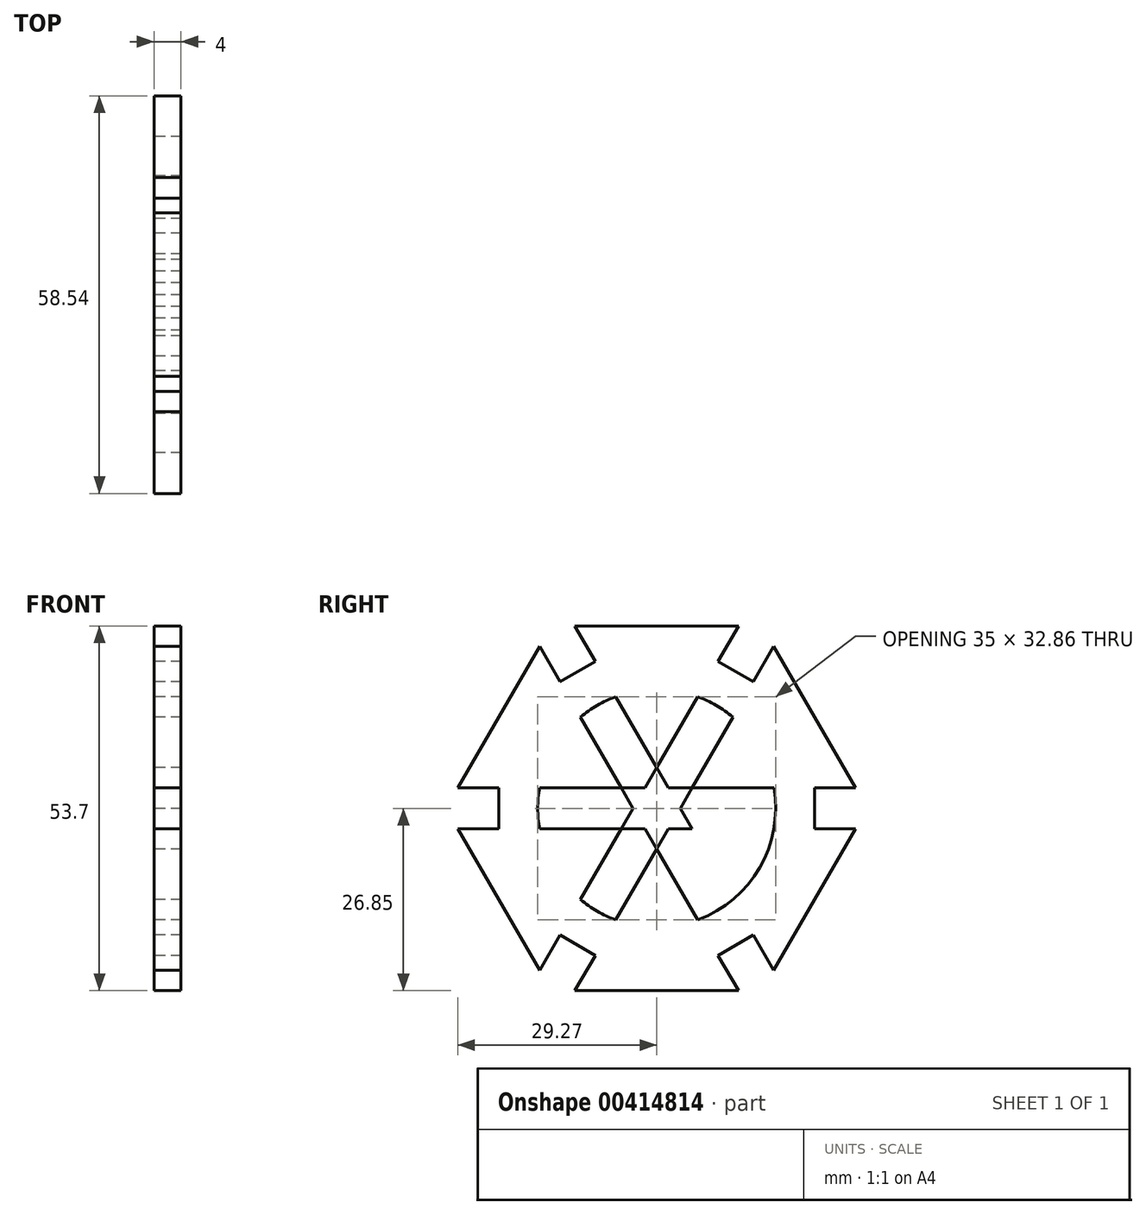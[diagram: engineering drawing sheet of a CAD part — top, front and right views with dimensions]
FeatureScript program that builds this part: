
annotation { "Feature Type Name" : "Feature", "Feature Type Description" : "" }
export const myFeature = defineFeature(function(context is Context, id is Id, definition is map)
    precondition{}
    {
        {
            var Q0;
            Q0=qCreatedBy(makeId("Right.planeOp"),FACE);
            var sketch = newSketch(context, id + "F0", { "sketchPlane" : qUnion([Q0])});
            skCircle(sketch, "E0.cCircle", {"center": v(0, 0) * mm, "radius": 31 * mm, "construction": true});
            skLineSegment(sketch, "E0.0", {"start": v(31, 0) * mm, "end": v(15.5, -26.85) * mm});
            skLineSegment(sketch, "E0.1", {"start": v(15.5, -26.85) * mm, "end": v(-15.5, -26.85) * mm});
            skLineSegment(sketch, "E0.2", {"start": v(-15.5, -26.85) * mm, "end": v(-31, 0) * mm});
            skLineSegment(sketch, "E0.3", {"start": v(-31, 0) * mm, "end": v(-15.5, 26.85) * mm});
            skLineSegment(sketch, "E0.4", {"start": v(-15.5, 26.85) * mm, "end": v(15.5, 26.85) * mm});
            skLineSegment(sketch, "E0.5", {"start": v(15.5, 26.85) * mm, "end": v(31, 0) * mm});
            skLineSegment(sketch, "E1", {"start": v(-31, 0) * mm, "end": v(31, 0) * mm, "construction": true});
            skLineSegment(sketch, "E2", {"start": v(-15.5, 26.85) * mm, "end": v(15.5, -26.85) * mm, "construction": true});
            skLineSegment(sketch, "E3", {"start": v(15.5, 26.85) * mm, "end": v(-15.5, -26.85) * mm, "construction": true});
            skCircle(sketch, "E4.cCircle", {"center": v(0, 0) * mm, "radius": 17.5 * mm});
            skPoint(sketch, "E4.0.midPoint", {"position": v(15.16, 8.75) * mm});
            skLineSegment(sketch, "E5", {"start": v(-11.22, 13.43) * mm, "end": v(6.02, -16.43) * mm});
            skLineSegment(sketch, "E6.MirrorCS", {"start": v(-6.02, 16.43) * mm, "end": v(11.22, -13.43) * mm});
            skLineSegment(sketch, "E7", {"start": v(-17.24, 3) * mm, "end": v(17.24, 3) * mm});
            skLineSegment(sketch, "E8.MirrorCS", {"start": v(-17.24, -3) * mm, "end": v(17.24, -3) * mm});
            skLineSegment(sketch, "E9", {"start": v(-11.22, -13.43) * mm, "end": v(6.02, 16.43) * mm});
            skLineSegment(sketch, "E10.MirrorCS", {"start": v(-6.02, -16.43) * mm, "end": v(11.22, 13.43) * mm});
            skLineSegment(sketch, "E11", {"start": v(-17.23, 23.85) * mm, "end": v(-14.23, 18.65) * mm});
            skLineSegment(sketch, "E12.MirrorCS", {"start": v(-12.04, 26.85) * mm, "end": v(-9.04, 21.65) * mm});
            skLineSegment(sketch, "E13", {"start": v(-14.23, 18.65) * mm, "end": v(-9.04, 21.65) * mm});
            skLineSegment(sketch, "E14.MirrorCS", {"start": v(14.23, 18.65) * mm, "end": v(9.04, 21.65) * mm});
            skLineSegment(sketch, "E15.MirrorCS", {"start": v(17.23, 23.85) * mm, "end": v(14.23, 18.65) * mm});
            skLineSegment(sketch, "E16.MirrorCS", {"start": v(12.04, 26.85) * mm, "end": v(9.04, 21.65) * mm});
            skLineSegment(sketch, "E17.MirrorCS", {"start": v(-12.04, -26.85) * mm, "end": v(-9.04, -21.65) * mm});
            skLineSegment(sketch, "E18.MirrorCS", {"start": v(-14.23, -18.65) * mm, "end": v(-9.04, -21.65) * mm});
            skLineSegment(sketch, "E19.MirrorCS", {"start": v(-17.23, -23.85) * mm, "end": v(-14.23, -18.65) * mm});
            skLineSegment(sketch, "E20.MirrorCS", {"start": v(12.04, -26.85) * mm, "end": v(9.04, -21.65) * mm});
            skLineSegment(sketch, "E21.MirrorCS", {"start": v(14.23, -18.65) * mm, "end": v(9.04, -21.65) * mm});
            skLineSegment(sketch, "E22.MirrorCS", {"start": v(17.23, -23.85) * mm, "end": v(14.23, -18.65) * mm});
            skLineSegment(sketch, "E23", {"start": v(0, 0) * mm, "end": v(-23.25, 13.42) * mm, "construction": true});
            skLineSegment(sketch, "E24.MirrorCS", {"start": v(-29.27, 3) * mm, "end": v(-23.27, 3) * mm});
            skLineSegment(sketch, "E25.MirrorCS", {"start": v(-29.27, -3) * mm, "end": v(-23.27, -3) * mm});
            skLineSegment(sketch, "E26.MirrorCS", {"start": v(-23.27, 3) * mm, "end": v(-23.27, -3) * mm});
            skLineSegment(sketch, "E27.MirrorCS", {"start": v(23.27, 3) * mm, "end": v(23.27, -3) * mm});
            skLineSegment(sketch, "E28.MirrorCS", {"start": v(29.27, -3) * mm, "end": v(23.27, -3) * mm});
            skLineSegment(sketch, "E29.MirrorCS", {"start": v(29.27, 3) * mm, "end": v(23.27, 3) * mm});
            skSolve(sketch);
        }
        {
            var Q0;
            {var subQ4=sQuery(id+"F0.wireOp",EDGE,"E11");Q0=makeQuery(id+"F0.imprint","IMPRINT",FACE,{"disambiguationData":[TD([[makeQuery(id+"F0.imprint","IMPRINT",EDGE,{"derivedFrom":subQ4}),-1.0]])]});}
            var Q1;
            {var subQ1=sQuery(id+"F0.wireOp",EDGE,"E4.cCircle");var subQ5=sQuery(id+"F0.wireOp",EDGE,"E5");var subQ6=makeQuery(id+"F0.imprint","INTERSECT",VERTEX,{"disambiguationData":[OD(0.0)],"derivedFrom":[subQ1,subQ5]});Q1=makeQuery(id+"F0.imprint","IMPRINT",FACE,{"disambiguationData":[TD([[makeQuery(id+"F0.imprint","IMPRINT",EDGE,{"disambiguationData":[TD([[subQ6,1.0]])],"derivedFrom":subQ1}),1.0]])]});}
            var Q2;
            {var subQ5=sQuery(id+"F0.wireOp",EDGE,"E9");var subQ6=sQuery(id+"F0.wireOp",EDGE,"E4.cCircle");var subQ7=makeQuery(id+"F0.imprint","INTERSECT",VERTEX,{"disambiguationData":[OD(1.0)],"derivedFrom":[subQ6,subQ5]});Q2=makeQuery(id+"F0.imprint","IMPRINT",FACE,{"disambiguationData":[TD([[makeQuery(id+"F0.imprint","IMPRINT",EDGE,{"disambiguationData":[TD([[subQ7,1.0]])],"derivedFrom":subQ6}),1.0]])]});}
            var Q3;
            {var subQ5=sQuery(id+"F0.wireOp",EDGE,"E4.cCircle");var subQ7=sQuery(id+"F0.wireOp",EDGE,"E7");var subQ8=makeQuery(id+"F0.imprint","INTERSECT",VERTEX,{"disambiguationData":[OD(1.0)],"derivedFrom":[subQ5,subQ7]});Q3=makeQuery(id+"F0.imprint","IMPRINT",FACE,{"disambiguationData":[TD([[makeQuery(id+"F0.imprint","IMPRINT",EDGE,{"disambiguationData":[TD([[subQ8,1.0]])],"derivedFrom":subQ5}),1.0]])]});}
            var Q4;
            {var subQ5=sQuery(id+"F0.wireOp",EDGE,"E4.cCircle");var subQ7=sQuery(id+"F0.wireOp",EDGE,"E5");var subQ8=makeQuery(id+"F0.imprint","INTERSECT",VERTEX,{"disambiguationData":[OD(1.0)],"derivedFrom":[subQ5,subQ7]});Q4=makeQuery(id+"F0.imprint","IMPRINT",FACE,{"disambiguationData":[TD([[makeQuery(id+"F0.imprint","IMPRINT",EDGE,{"disambiguationData":[TD([[subQ8,-1.0]])],"derivedFrom":subQ5}),1.0]])]});}
            var Q5;
            {var subQ3=sQuery(id+"F0.wireOp",EDGE,"E9");var subQ7=sQuery(id+"F0.wireOp",EDGE,"E4.cCircle");var subQ9=makeQuery(id+"F0.imprint","INTERSECT",VERTEX,{"disambiguationData":[OD(0.0)],"derivedFrom":[subQ7,subQ3]});Q5=makeQuery(id+"F0.imprint","IMPRINT",FACE,{"disambiguationData":[TD([[makeQuery(id+"F0.imprint","IMPRINT",EDGE,{"disambiguationData":[TD([[subQ9,-1.0]])],"derivedFrom":subQ7}),1.0]])]});}
            var Q6;
            {var subQ1=sQuery(id+"F0.wireOp",EDGE,"E4.cCircle");var subQ5=sQuery(id+"F0.wireOp",EDGE,"E7");var subQ6=makeQuery(id+"F0.imprint","INTERSECT",VERTEX,{"disambiguationData":[OD(0.0)],"derivedFrom":[subQ1,subQ5]});Q6=makeQuery(id+"F0.imprint","IMPRINT",FACE,{"disambiguationData":[TD([[makeQuery(id+"F0.imprint","IMPRINT",EDGE,{"disambiguationData":[TD([[subQ6,-1.0]])],"derivedFrom":subQ1}),1.0]])]});}
            var Q7;
            {var subQ0=sQuery(id+"F0.wireOp",EDGE,"E8.MirrorCS");var subQ1=sQuery(id+"F0.wireOp",EDGE,"E5");var subQ2=makeQuery(id+"F0.imprint","INTERSECT",VERTEX,{"derivedFrom":[subQ1,subQ0]});Q7=makeQuery(id+"F0.imprint","IMPRINT",FACE,{"disambiguationData":[TD([[makeQuery(id+"F0.imprint","IMPRINT",EDGE,{"disambiguationData":[TD([[subQ2,-1.0]])],"derivedFrom":subQ1}),1.0]])]});}
            var Q8;
            {var subQ0=sQuery(id+"F0.wireOp",EDGE,"E10.MirrorCS");var subQ1=sQuery(id+"F0.wireOp",EDGE,"E6.MirrorCS");var subQ2=makeQuery(id+"F0.imprint","INTERSECT",VERTEX,{"derivedFrom":[subQ1,subQ0]});Q8=makeQuery(id+"F0.imprint","IMPRINT",FACE,{"disambiguationData":[TD([[makeQuery(id+"F0.imprint","IMPRINT",EDGE,{"disambiguationData":[TD([[subQ2,-1.0]])],"derivedFrom":subQ1}),-1.0]])]});}
            var Q9;
            {var subQ0=sQuery(id+"F0.wireOp",EDGE,"E7");var subQ1=sQuery(id+"F0.wireOp",EDGE,"E6.MirrorCS");var subQ2=makeQuery(id+"F0.imprint","INTERSECT",VERTEX,{"derivedFrom":[subQ1,subQ0]});Q9=makeQuery(id+"F0.imprint","IMPRINT",FACE,{"disambiguationData":[TD([[makeQuery(id+"F0.imprint","IMPRINT",EDGE,{"disambiguationData":[TD([[subQ2,-1.0]])],"derivedFrom":subQ1}),1.0]])]});}
            var Q10;
            {var subQ0=sQuery(id+"F0.wireOp",EDGE,"E9");var subQ1=sQuery(id+"F0.wireOp",EDGE,"E6.MirrorCS");var subQ2=makeQuery(id+"F0.imprint","INTERSECT",VERTEX,{"derivedFrom":[subQ1,subQ0]});Q10=makeQuery(id+"F0.imprint","IMPRINT",FACE,{"disambiguationData":[TD([[makeQuery(id+"F0.imprint","IMPRINT",EDGE,{"disambiguationData":[TD([[subQ2,-1.0]])],"derivedFrom":subQ1}),-1.0]])]});}
            var Q11;
            {var subQ0=sQuery(id+"F0.wireOp",EDGE,"E7");var subQ1=sQuery(id+"F0.wireOp",EDGE,"E5");var subQ2=makeQuery(id+"F0.imprint","INTERSECT",VERTEX,{"derivedFrom":[subQ1,subQ0]});Q11=makeQuery(id+"F0.imprint","IMPRINT",FACE,{"disambiguationData":[TD([[makeQuery(id+"F0.imprint","IMPRINT",EDGE,{"disambiguationData":[TD([[subQ2,-1.0]])],"derivedFrom":subQ1}),1.0]])]});}
            var Q12;
            {var subQ0=sQuery(id+"F0.wireOp",EDGE,"E9");var subQ1=sQuery(id+"F0.wireOp",EDGE,"E5");var subQ2=makeQuery(id+"F0.imprint","INTERSECT",VERTEX,{"derivedFrom":[subQ1,subQ0]});Q12=makeQuery(id+"F0.imprint","IMPRINT",FACE,{"disambiguationData":[TD([[makeQuery(id+"F0.imprint","IMPRINT",EDGE,{"disambiguationData":[TD([[subQ2,-1.0]])],"derivedFrom":subQ1}),-1.0]])]});}
            var Q13;
            {var subQ1=sQuery(id+"F0.wireOp",EDGE,"E5");var subQ8=sQuery(id+"F0.wireOp",EDGE,"E9");var subQ11=makeQuery(id+"F0.imprint","INTERSECT",VERTEX,{"derivedFrom":[subQ1,subQ8]});Q13=makeQuery(id+"F0.imprint","IMPRINT",FACE,{"disambiguationData":[TD([[makeQuery(id+"F0.imprint","IMPRINT",EDGE,{"disambiguationData":[TD([[subQ11,-1.0]])],"derivedFrom":subQ1}),1.0]])]});}
            extrude(context, id + "F1", {"entities" : qUnion([Q0, Q1, Q2, Q3, Q4, Q5, Q6, Q7, Q8, Q9, Q10, Q11, Q12, Q13]), "depth" : 4 * mm, "offsetDistance" : 25 * mm});
        }
    });
